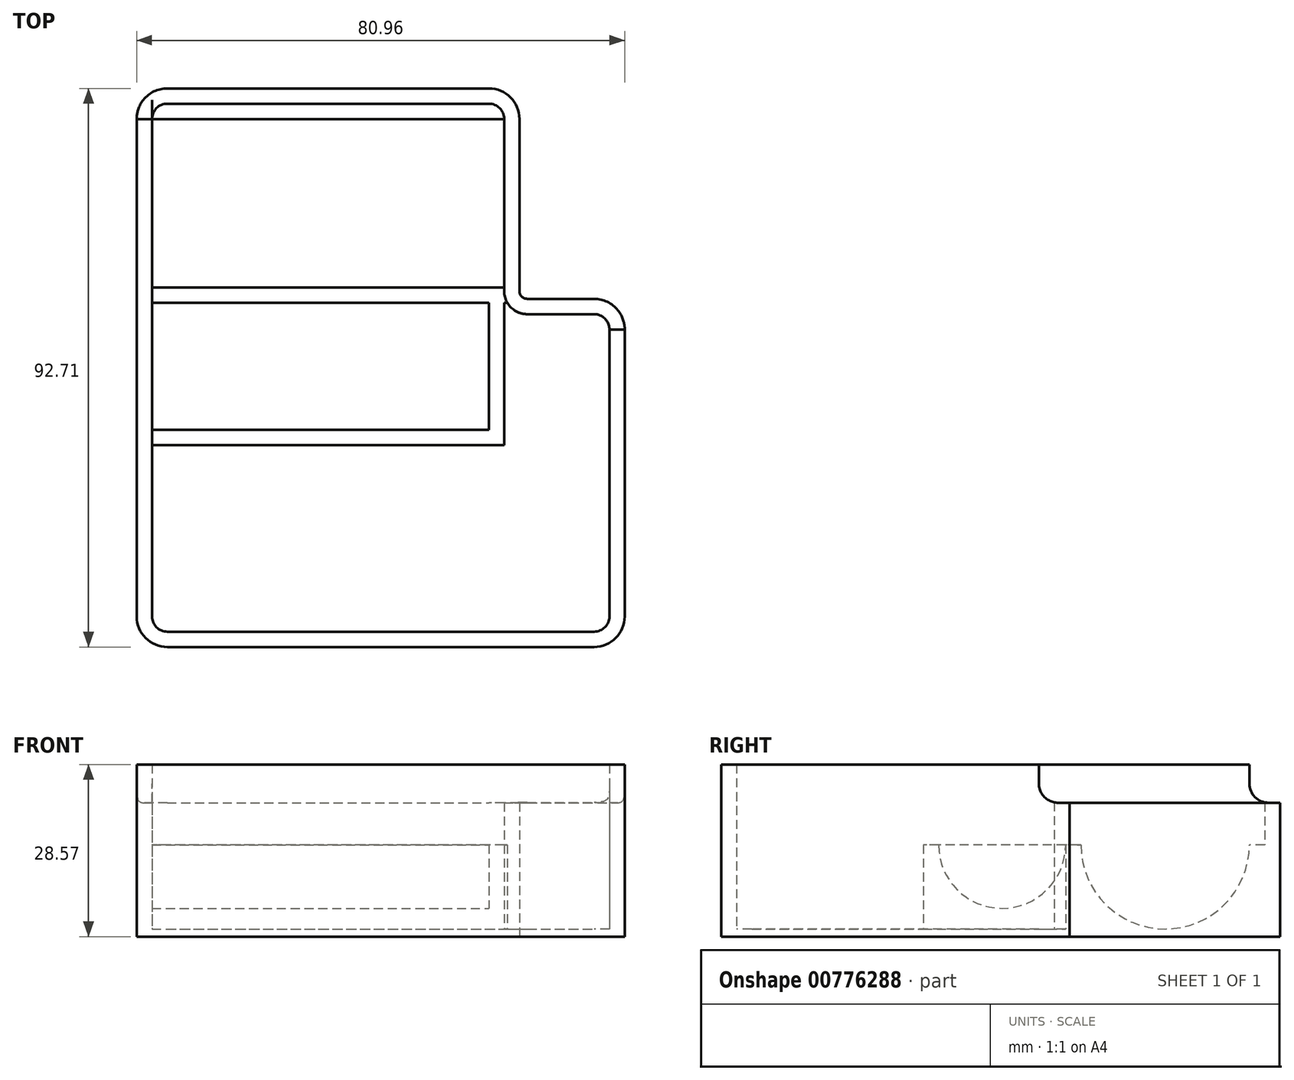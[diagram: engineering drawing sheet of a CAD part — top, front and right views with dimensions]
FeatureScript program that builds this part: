
annotation { "Feature Type Name" : "Feature", "Feature Type Description" : "" }
export const myFeature = defineFeature(function(context is Context, id is Id, definition is map)
    precondition{}
    {
        {
            var Q0;
            Q0=qCreatedBy(makeId("Top.planeOp"),FACE);
            var sketch = newSketch(context, id + "F0", { "sketchPlane" : qUnion([Q0])});
            skLineSegment(sketch, "E0", {"start": v(5.08, 92.7) * mm, "end": v(58.42, 92.7) * mm});
            skLineSegment(sketch, "E1", {"start": v(63.5, 87.63) * mm, "end": v(63.5, 59.05) * mm});
            skLineSegment(sketch, "E2", {"start": v(64.77, 57.78) * mm, "end": v(75.88, 57.79) * mm});
            skLineSegment(sketch, "E3", {"start": v(80.96, 52.7) * mm, "end": v(80.96, 5.08) * mm});
            skLineSegment(sketch, "E4", {"start": v(0, 5.08) * mm, "end": v(0, 87.63) * mm});
            skLineSegment(sketch, "E5", {"start": v(5.08, 0) * mm, "end": v(75.88, 0) * mm});
            skLineSegment(sketch, "E6.0", {"start": v(5.08, 2.54) * mm, "end": v(75.88, 2.54) * mm});
            skLineSegment(sketch, "E6.1", {"start": v(5.08, 90.17) * mm, "end": v(58.42, 90.17) * mm});
            skLineSegment(sketch, "E6.2", {"start": v(60.96, 87.63) * mm, "end": v(60.96, 59.05) * mm});
            skLineSegment(sketch, "E6.3", {"start": v(2.54, 5.08) * mm, "end": v(2.54, 87.63) * mm});
            skLineSegment(sketch, "E6.4", {"start": v(64.77, 55.24) * mm, "end": v(75.88, 55.25) * mm});
            skLineSegment(sketch, "E6.5", {"start": v(78.42, 52.7) * mm, "end": v(78.42, 5.08) * mm});
            skPoint(sketch, "E7.visualSharp", {"position": v(2.54, 90.17) * mm});
            skArc(sketch, "E7.filletArc", {"start": v(5.08, 90.17) * mm, "mid": v(3.28, 89.43) * mm, "end": v(2.54, 87.63) * mm});
            skPoint(sketch, "E8.visualSharp", {"position": v(60.96, 90.17) * mm});
            skArc(sketch, "E8.filletArc", {"start": v(60.96, 87.63) * mm, "mid": v(60.22, 89.43) * mm, "end": v(58.42, 90.17) * mm});
            skPoint(sketch, "E9.visualSharp", {"position": v(78.42, 55.25) * mm});
            skArc(sketch, "E9.filletArc", {"start": v(78.42, 52.7) * mm, "mid": v(77.68, 54.5) * mm, "end": v(75.88, 55.25) * mm});
            skPoint(sketch, "E10.visualSharp", {"position": v(2.54, 2.54) * mm});
            skArc(sketch, "E10.filletArc", {"start": v(2.54, 5.08) * mm, "mid": v(3.28, 3.28) * mm, "end": v(5.08, 2.54) * mm});
            skPoint(sketch, "E11.visualSharp", {"position": v(78.42, 2.54) * mm});
            skArc(sketch, "E11.filletArc", {"start": v(75.88, 2.54) * mm, "mid": v(77.68, 3.28) * mm, "end": v(78.42, 5.08) * mm});
            skPoint(sketch, "E12.visualSharp", {"position": v(0, 92.7) * mm});
            skArc(sketch, "E12.filletArc", {"start": v(5.08, 92.7) * mm, "mid": v(1.49, 91.22) * mm, "end": v(0, 87.63) * mm});
            skPoint(sketch, "E13.visualSharp", {"position": v(63.5, 92.7) * mm});
            skArc(sketch, "E13.filletArc", {"start": v(63.5, 87.63) * mm, "mid": v(62.01, 91.22) * mm, "end": v(58.42, 92.7) * mm});
            skPoint(sketch, "E14.visualSharp", {"position": v(0, 0) * mm});
            skArc(sketch, "E14.filletArc", {"start": v(0, 5.08) * mm, "mid": v(1.49, 1.49) * mm, "end": v(5.08, 0) * mm});
            skPoint(sketch, "E15.visualSharp", {"position": v(80.96, 0) * mm});
            skArc(sketch, "E15.filletArc", {"start": v(75.88, 0) * mm, "mid": v(79.47, 1.49) * mm, "end": v(80.96, 5.08) * mm});
            skPoint(sketch, "E16.visualSharp", {"position": v(60.96, 55.24) * mm});
            skArc(sketch, "E16.filletArc", {"start": v(60.96, 59.05) * mm, "mid": v(62.08, 56.36) * mm, "end": v(64.77, 55.24) * mm});
            skPoint(sketch, "E17.visualSharp", {"position": v(80.96, 57.79) * mm});
            skArc(sketch, "E17.filletArc", {"start": v(80.96, 52.7) * mm, "mid": v(79.47, 56.3) * mm, "end": v(75.88, 57.79) * mm});
            skPoint(sketch, "E18.visualSharp", {"position": v(63.5, 57.78) * mm});
            skArc(sketch, "E18.filletArc", {"start": v(63.5, 59.05) * mm, "mid": v(63.87, 58.16) * mm, "end": v(64.77, 57.78) * mm});
            skSolve(sketch);
        }
        {
            var Q0;
            Q0=makeQuery(id+"F0.imprint","IMPRINT",FACE,{"disambiguationData":[TD([[makeQuery(id+"F0.imprint","IMPRINT",EDGE,{"derivedFrom":sQuery(id+"F0.wireOp",EDGE,"E0")}),-1.0]])]});
            extrude(context, id + "F1", {"entities" : qUnion([Q0]), "depth" : 28.57 * mm, "offsetDistance" : 25.4 * mm});
        }
        {
            var Q0;
            Q0=qCreatedBy(makeId("Right.planeOp"),FACE);
            cPlane(context, id + "F2", {"entities" : qUnion([Q0]), "cplaneType" : CPlaneType.OFFSET, "offset" : 25.4 * mm, "width" : 152.4 * mm, "height" : 152.4 * mm});
        }
        {
            var Q0;
            Q0=qCreatedBy(id+"F2.planeOp",FACE);
            var sketch = newSketch(context, id + "F3", { "sketchPlane" : qUnion([Q0])});
            skLineSegment(sketch, "E19", {"start": v(57.15, 15.24) * mm, "end": v(57.15, 0) * mm});
            skLineSegment(sketch, "E20", {"start": v(57.15, 15.24) * mm, "end": v(59.69, 15.24) * mm});
            skLineSegment(sketch, "E21", {"start": v(59.69, 15.24) * mm, "end": v(87.63, 15.24) * mm, "construction": true});
            skLineSegment(sketch, "E22", {"start": v(87.63, 15.24) * mm, "end": v(90.17, 15.24) * mm});
            skPoint(sketch, "E23.0.start.orphan", {"position": v(90.17, 28.58) * mm});
            skLineSegment(sketch, "E24.0", {"start": v(90.17, 28.58) * mm, "end": v(90.17, 0) * mm, "construction": true});
            skArc(sketch, "E25", {"start": v(59.69, 15.24) * mm, "mid": v(73.66, 29.21) * mm, "end": v(87.63, 15.24) * mm, "construction": true});
            skLineSegment(sketch, "E26", {"start": v(73.66, 1.27) * mm, "end": v(73.66, 0) * mm});
            skLineSegment(sketch, "E27", {"start": v(73.66, 15.24) * mm, "end": v(73.66, 0) * mm, "construction": true});
            skArc(sketch, "E28.trimOffspring", {"start": v(73.66, 1.27) * mm, "mid": v(83.54, 5.36) * mm, "end": v(87.63, 15.24) * mm});
            skArc(sketch, "E29", {"start": v(59.69, 15.24) * mm, "mid": v(63.78, 5.36) * mm, "end": v(73.66, 1.27) * mm});
            skLineSegment(sketch, "E30.trimOffspring", {"start": v(73.66, 0) * mm, "end": v(90.17, 0) * mm});
            skLineSegment(sketch, "E31", {"start": v(57.15, 0) * mm, "end": v(73.66, 0) * mm});
            skLineSegment(sketch, "E32", {"start": v(73.66, 0) * mm, "end": v(73.66, 0) * mm});
            skLineSegment(sketch, "E33", {"start": v(90.17, 15.24) * mm, "end": v(90.17, 0) * mm});
            skSolve(sketch);
        }
        {
            var Q0;
            Q0=makeQuery(id+"F3.imprint","IMPRINT",FACE,{"disambiguationData":[TD([[makeQuery(id+"F3.imprint","IMPRINT",EDGE,{"derivedFrom":sQuery(id+"F3.wireOp",EDGE,"E22")}),-1.0]])]});
            var Q1;
            Q1=makeQuery(id+"F3.imprint","IMPRINT",FACE,{"disambiguationData":[TD([[makeQuery(id+"F3.imprint","IMPRINT",EDGE,{"derivedFrom":sQuery(id+"F3.wireOp",EDGE,"E19")}),1.0]])]});
            extrude(context, id + "F4", {"entities" : qUnion([Q0, Q1]), "operationType" : NewBodyOperationType.ADD, "endBound" : BoundingType.UP_TO_NEXT, "depth" : 25.4 * mm, "offsetDistance" : 25.4 * mm, "hasSecondDirection" : true, "secondDirectionBound" : SecondDirectionBoundingType.UP_TO_NEXT, "secondDirectionOppositeDirection" : true, "secondDirectionDepth" : 25.4 * mm});
        }
        {
            var Q0;
            Q0=qCreatedBy(id+"F2.planeOp",FACE);
            var sketch = newSketch(context, id + "F5", { "sketchPlane" : qUnion([Q0])});
            skLineSegment(sketch, "E34.0", {"start": v(57.15, 15.24) * mm, "end": v(57.15, 0) * mm});
            skArc(sketch, "E35", {"start": v(57.15, 15.24) * mm, "mid": v(46.6, 4.7) * mm, "end": v(36.07, 15.24) * mm});
            skLineSegment(sketch, "E36", {"start": v(36.07, 15.24) * mm, "end": v(33.53, 15.24) * mm});
            skLineSegment(sketch, "E37", {"start": v(33.53, 15.24) * mm, "end": v(33.53, 0) * mm});
            skLineSegment(sketch, "E38", {"start": v(33.53, 0) * mm, "end": v(57.15, 0) * mm});
            skSolve(sketch);
        }
        {
            var Q0;
            Q0=makeQuery(id+"F5.imprint","IMPRINT",FACE,{"disambiguationData":[TD([[makeQuery(id+"F5.imprint","IMPRINT",EDGE,{"derivedFrom":sQuery(id+"F5.wireOp",EDGE,"E34.0")}),-1.0]])]});
            extrude(context, id + "F6", {"entities" : qUnion([Q0]), "operationType" : NewBodyOperationType.ADD, "endBound" : BoundingType.UP_TO_NEXT, "oppositeDirection" : true, "depth" : 25.4 * mm, "offsetDistance" : 25.4 * mm, "hasSecondDirection" : true, "secondDirectionOppositeDirection" : false, "secondDirectionDepth" : 33.02 * mm});
        }
        {
            var Q0;
            Q0=makeQuery(id+"F6.opExtrude","CAP_FACE",FACE,{"disambiguationData":[OSD([sQuery(id+"F5.wireOp",EDGE,"E34.0"),sQuery(id+"F5.wireOp",EDGE,"E35"),sQuery(id+"F5.wireOp",EDGE,"E36"),sQuery(id+"F5.wireOp",EDGE,"E37"),sQuery(id+"F5.wireOp",EDGE,"E38")])],"isStart":true});
            var sketch = newSketch(context, id + "F7", { "sketchPlane" : qUnion([Q0])});
            skLineSegment(sketch, "E39.0", {"start": v(57.15, 15.24) * mm, "end": v(57.15, 0) * mm});
            skLineSegment(sketch, "E40.0", {"start": v(33.53, 15.24) * mm, "end": v(33.53, 0) * mm});
            skLineSegment(sketch, "E41", {"start": v(33.53, 15.24) * mm, "end": v(57.15, 15.24) * mm});
            skLineSegment(sketch, "E42", {"start": v(33.53, 0) * mm, "end": v(57.15, 0) * mm});
            skSolve(sketch);
        }
        {
            var Q0;
            Q0 = qSketchRegion(id + "F7", true);
            extrude(context, id + "F8", {"entities" : qUnion([Q0]), "operationType" : NewBodyOperationType.ADD, "depth" : 2.54 * mm, "offsetDistance" : 25.4 * mm});
        }
        {
            var Q0;
            Q0=qCreatedBy(makeId("Top.planeOp"),FACE);
            var sketch = newSketch(context, id + "F9", { "sketchPlane" : qUnion([Q0])});
            skArc(sketch, "E43.0", {"start": v(60.96, 59.05) * mm, "mid": v(62.08, 56.36) * mm, "end": v(64.77, 55.24) * mm});
            skLineSegment(sketch, "E44.0", {"start": v(64.77, 55.24) * mm, "end": v(75.88, 55.25) * mm});
            skArc(sketch, "E45.0", {"start": v(78.42, 52.7) * mm, "mid": v(77.68, 54.5) * mm, "end": v(75.88, 55.25) * mm});
            skLineSegment(sketch, "E46.0", {"start": v(78.42, 52.7) * mm, "end": v(78.42, 5.08) * mm});
            skLineSegment(sketch, "E47.0", {"start": v(61.47, 57.15) * mm, "end": v(60.96, 57.15) * mm});
            skLineSegment(sketch, "E48.0", {"start": v(60.96, 33.53) * mm, "end": v(60.96, 57.15) * mm});
            skLineSegment(sketch, "E49.0", {"start": v(2.54, 33.53) * mm, "end": v(60.96, 33.53) * mm});
            skArc(sketch, "E50.0", {"start": v(2.54, 5.08) * mm, "mid": v(3.28, 3.28) * mm, "end": v(5.08, 2.54) * mm});
            skLineSegment(sketch, "E51.0", {"start": v(5.08, 2.54) * mm, "end": v(75.88, 2.54) * mm});
            skArc(sketch, "E52.0", {"start": v(75.88, 2.54) * mm, "mid": v(77.68, 3.28) * mm, "end": v(78.42, 5.08) * mm});
            skLineSegment(sketch, "E53", {"start": v(2.54, 5.08) * mm, "end": v(2.54, 33.53) * mm});
            skSolve(sketch);
        }
        {
            var Q0;
            {var subQ1=sQuery(id+"F9.wireOp",EDGE,"E44.0");Q0=makeQuery(id+"F9.imprint","IMPRINT",FACE,{"disambiguationData":[TD([[makeQuery(id+"F9.imprint","IMPRINT",EDGE,{"derivedFrom":subQ1}),-1.0]])]});}
            extrude(context, id + "F10", {"entities" : qUnion([Q0]), "operationType" : NewBodyOperationType.ADD, "depth" : 1.27 * mm, "offsetDistance" : 25.4 * mm});
        }
        {
            var Q0;
            Q0=makeQuery(id+"F1.opExtrude","CAP_FACE",FACE,{"disambiguationData":[OSD([sQuery(id+"F0.wireOp",EDGE,"E0"),sQuery(id+"F0.wireOp",EDGE,"E1"),sQuery(id+"F0.wireOp",EDGE,"E2"),sQuery(id+"F0.wireOp",EDGE,"E3"),sQuery(id+"F0.wireOp",EDGE,"E4"),sQuery(id+"F0.wireOp",EDGE,"E5"),sQuery(id+"F0.wireOp",EDGE,"E6.0"),sQuery(id+"F0.wireOp",EDGE,"E6.1"),sQuery(id+"F0.wireOp",EDGE,"E6.2"),sQuery(id+"F0.wireOp",EDGE,"E6.3"),sQuery(id+"F0.wireOp",EDGE,"E6.4"),sQuery(id+"F0.wireOp",EDGE,"E6.5"),sQuery(id+"F0.wireOp",EDGE,"E7.filletArc"),sQuery(id+"F0.wireOp",EDGE,"E8.filletArc"),sQuery(id+"F0.wireOp",EDGE,"E9.filletArc"),sQuery(id+"F0.wireOp",EDGE,"E10.filletArc"),sQuery(id+"F0.wireOp",EDGE,"E11.filletArc"),sQuery(id+"F0.wireOp",EDGE,"E12.filletArc"),sQuery(id+"F0.wireOp",EDGE,"E13.filletArc"),sQuery(id+"F0.wireOp",EDGE,"E14.filletArc"),sQuery(id+"F0.wireOp",EDGE,"E15.filletArc"),sQuery(id+"F0.wireOp",EDGE,"E16.filletArc"),sQuery(id+"F0.wireOp",EDGE,"E17.filletArc"),sQuery(id+"F0.wireOp",EDGE,"E18.filletArc")])],"isStart":false});
            var sketch = newSketch(context, id + "F11", { "sketchPlane" : qUnion([Q0])});
            skArc(sketch, "E54.0.1", {"start": v(80.96, 52.7) * mm, "mid": v(79.47, 56.3) * mm, "end": v(75.88, 57.79) * mm});
            skLineSegment(sketch, "E54.0.2", {"start": v(75.88, 57.79) * mm, "end": v(64.77, 57.78) * mm});
            skArc(sketch, "E54.0.3", {"start": v(64.77, 57.79) * mm, "mid": v(63.87, 58.16) * mm, "end": v(63.5, 59.05) * mm});
            skLineSegment(sketch, "E54.0.4", {"start": v(63.5, 59.05) * mm, "end": v(63.5, 87.63) * mm});
            skArc(sketch, "E54.0.5", {"start": v(63.5, 87.63) * mm, "mid": v(62.01, 91.22) * mm, "end": v(58.42, 92.7) * mm});
            skLineSegment(sketch, "E54.0.6", {"start": v(58.42, 92.7) * mm, "end": v(5.08, 92.7) * mm});
            skArc(sketch, "E54.0.7", {"start": v(5.08, 92.7) * mm, "mid": v(1.49, 91.22) * mm, "end": v(0, 87.63) * mm});
            skLineSegment(sketch, "E55.0", {"start": v(60.96, 87.63) * mm, "end": v(60.96, 59.05) * mm});
            skLineSegment(sketch, "E56.0", {"start": v(5.08, 90.17) * mm, "end": v(58.42, 90.17) * mm});
            skArc(sketch, "E57.0", {"start": v(60.96, 87.63) * mm, "mid": v(60.22, 89.43) * mm, "end": v(58.42, 90.17) * mm});
            skArc(sketch, "E58.0", {"start": v(60.96, 59.05) * mm, "mid": v(62.08, 56.36) * mm, "end": v(64.77, 55.24) * mm});
            skLineSegment(sketch, "E59.0", {"start": v(64.77, 55.24) * mm, "end": v(75.88, 55.25) * mm});
            skArc(sketch, "E60.0", {"start": v(78.42, 52.7) * mm, "mid": v(77.68, 54.5) * mm, "end": v(75.88, 55.25) * mm});
            skArc(sketch, "E61.0", {"start": v(5.08, 90.17) * mm, "mid": v(3.28, 89.43) * mm, "end": v(2.54, 87.63) * mm});
            skLineSegment(sketch, "E62", {"start": v(0, 87.63) * mm, "end": v(2.54, 87.63) * mm});
            skLineSegment(sketch, "E63", {"start": v(78.42, 52.7) * mm, "end": v(80.96, 52.7) * mm});
            skSolve(sketch);
        }
        {
            var Q0;
            Q0=makeQuery(id+"F11.imprint","IMPRINT",FACE,{"disambiguationData":[TD([[makeQuery(id+"F11.imprint","IMPRINT",EDGE,{"derivedFrom":sQuery(id+"F11.wireOp",EDGE,"E54.0.1")}),1.0]])]});
            extrude(context, id + "F12", {"entities" : qUnion([Q0]), "operationType" : NewBodyOperationType.REMOVE, "oppositeDirection" : true, "depth" : 6.35 * mm, "offsetDistance" : 25.4 * mm});
        }
        {
            var Q0;
            Q0=makeQuery(id+"F12.boolean.opBoolean","COPY",EDGE,{"derivedFrom":makeQuery(id+"F12.opExtrude","CAP_EDGE",EDGE,{"disambiguationData":[OSD([sQuery(id+"F11.wireOp",EDGE,"E62")])],"isStart":false})});
            var Q1;
            Q1=makeQuery(id+"F12.boolean.opBoolean","COPY",EDGE,{"derivedFrom":makeQuery(id+"F12.opExtrude","CAP_EDGE",EDGE,{"disambiguationData":[OSD([sQuery(id+"F11.wireOp",EDGE,"E62")])],"isStart":true})});
            var Q2;
            Q2=makeQuery(id+"F12.boolean.opBoolean","COPY",EDGE,{"derivedFrom":makeQuery(id+"F12.opExtrude","CAP_EDGE",EDGE,{"disambiguationData":[OSD([sQuery(id+"F11.wireOp",EDGE,"E63")])],"isStart":false})});
            var Q3;
            Q3=makeQuery(id+"F12.boolean.opBoolean","COPY",EDGE,{"derivedFrom":makeQuery(id+"F12.opExtrude","CAP_EDGE",EDGE,{"disambiguationData":[OSD([sQuery(id+"F11.wireOp",EDGE,"E63")])],"isStart":true})});
            fillet(context, id + "F13", {"entities" : qUnion([Q0, Q1, Q2, Q3]), "radius" : 3.17 * mm, "tangentPropagation" : true, "allowEdgeOverflow" : false});
        }
    });
